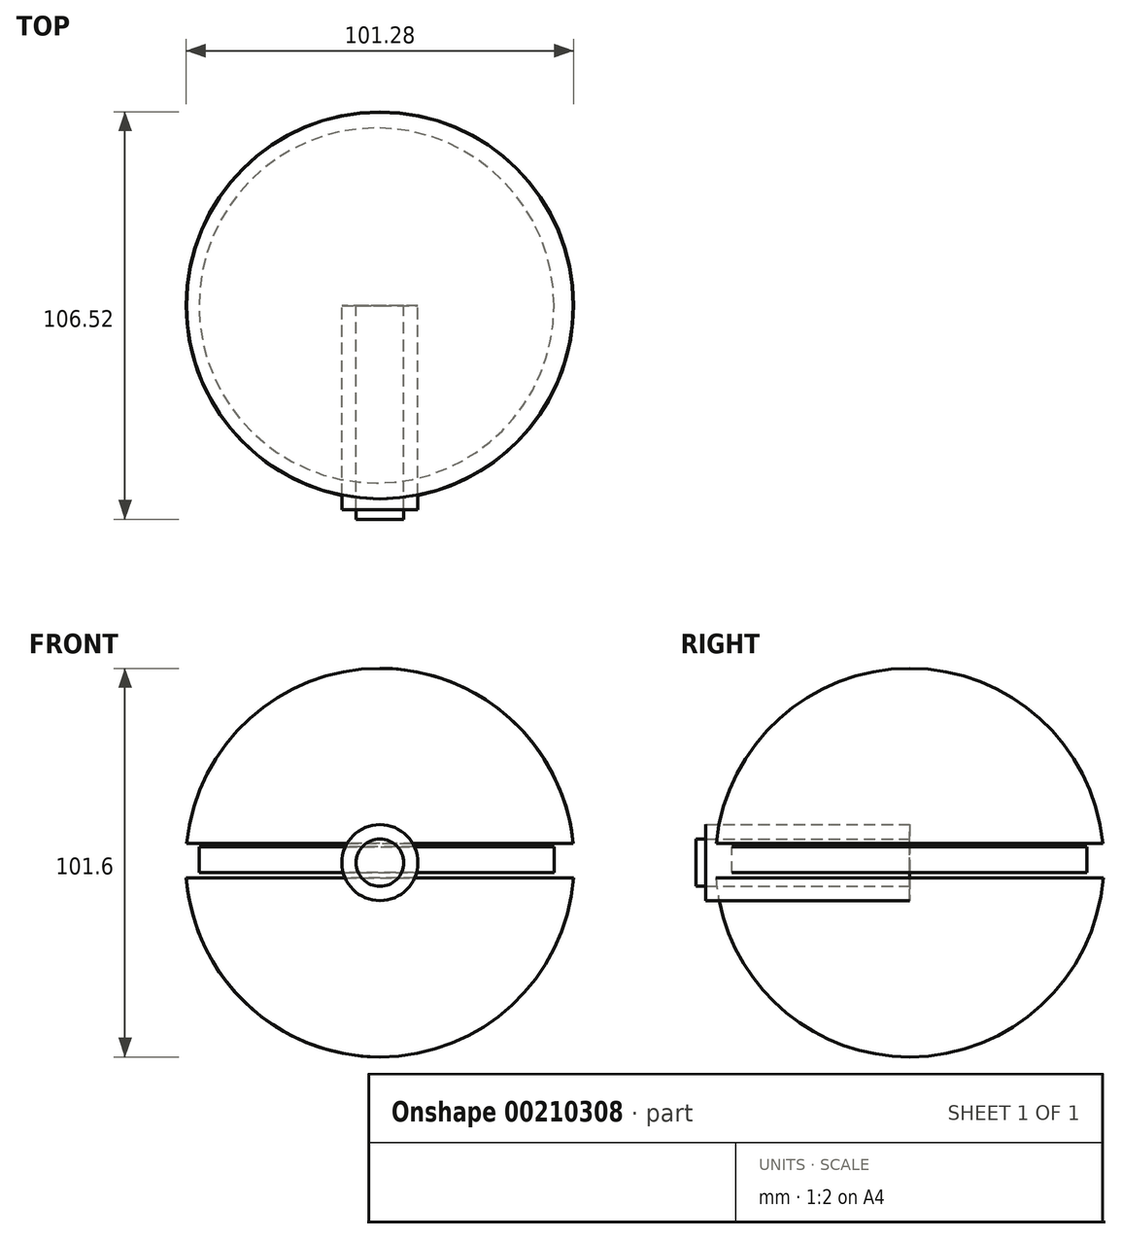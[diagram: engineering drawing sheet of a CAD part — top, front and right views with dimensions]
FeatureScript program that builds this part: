
annotation { "Feature Type Name" : "Feature", "Feature Type Description" : "" }
export const myFeature = defineFeature(function(context is Context, id is Id, definition is map)
    precondition{}
    {
        {
            var Q0;
            Q0=qCreatedBy(makeId("Front.planeOp"),FACE);
            var sketch = newSketch(context, id + "F0", { "sketchPlane" : qUnion([Q0])});
            skCircle(sketch, "E0", {"center": v(0, 0) * mm, "radius": 50.8 * mm});
            skLineSegment(sketch, "E1", {"start": v(-53.05, 5.08) * mm, "end": v(55.48, 5.08) * mm});
            skLineSegment(sketch, "E2", {"start": v(-52.82, -3.98) * mm, "end": v(55.03, -3.98) * mm});
            skLineSegment(sketch, "E3", {"start": v(0, 55.48) * mm, "end": v(0, -59.01) * mm});
            skSolve(sketch);
        }
        {
            var Q0;
            {var subQ0=sQuery(id+"F0.wireOp",EDGE,"E3");var subQ1=sQuery(id+"F0.wireOp",EDGE,"E0");var subQ2=makeQuery(id+"F0.imprint","INTERSECT",VERTEX,{"disambiguationData":[OD(0.0)],"derivedFrom":[subQ1,subQ0]});Q0=makeQuery(id+"F0.imprint","IMPRINT",FACE,{"disambiguationData":[TD([[makeQuery(id+"F0.imprint","IMPRINT",EDGE,{"disambiguationData":[TD([[subQ2,1.0]])],"derivedFrom":subQ1}),1.0]])]});}
            var Q1;
            {var subQ0=sQuery(id+"F0.wireOp",EDGE,"E2");var subQ1=sQuery(id+"F0.wireOp",EDGE,"E0");var subQ2=makeQuery(id+"F0.imprint","INTERSECT",VERTEX,{"disambiguationData":[OD(0.0)],"derivedFrom":[subQ1,subQ0]});Q1=makeQuery(id+"F0.imprint","IMPRINT",FACE,{"disambiguationData":[TD([[makeQuery(id+"F0.imprint","IMPRINT",EDGE,{"disambiguationData":[TD([[subQ2,-1.0]])],"derivedFrom":subQ1}),1.0]])]});}
            var Q2;
            Q2=sQuery(id+"F0.wireOp",EDGE,"E3");
            revolve(context, id + "F1", {"entities" : qUnion([Q0, Q1]), "axis" : qUnion([Q2]), "revolveType" : RevolveType.FULL});
        }
        {
            var Q0;
            Q0=qCreatedBy(makeId("Front.planeOp"),FACE);
            var sketch = newSketch(context, id + "F2", { "sketchPlane" : qUnion([Q0])});
            skLineSegment(sketch, "E4.bottom", {"start": v(-47.3, 4.2) * mm, "end": v(45.53, 4.2) * mm});
            skLineSegment(sketch, "E4.top", {"start": v(-47.3, -2.65) * mm, "end": v(45.53, -2.65) * mm});
            skLineSegment(sketch, "E4.left", {"start": v(-47.3, 4.2) * mm, "end": v(-47.3, -2.65) * mm});
            skLineSegment(sketch, "E4.right", {"start": v(45.53, 4.2) * mm, "end": v(45.53, -2.65) * mm});
            skLineSegment(sketch, "E5", {"start": v(-0.88, 4.2) * mm, "end": v(-0.88, -2.65) * mm});
            skSolve(sketch);
        }
        {
            var Q0;
            {var subQ0=sQuery(id+"F2.wireOp",EDGE,"E4.right");Q0=makeQuery(id+"F2.imprint","IMPRINT",FACE,{"disambiguationData":[TD([[makeQuery(id+"F2.imprint","IMPRINT",EDGE,{"derivedFrom":subQ0}),-1.0]])]});}
            var Q1;
            Q1=sQuery(id+"F2.wireOp",EDGE,"E5");
            revolve(context, id + "F3", {"entities" : qUnion([Q0]), "axis" : qUnion([Q1]), "revolveType" : RevolveType.FULL});
        }
        {
            var Q0;
            Q0=qCreatedBy(makeId("Front.planeOp"),FACE);
            var sketch = newSketch(context, id + "F4", { "sketchPlane" : qUnion([Q0])});
            skCircle(sketch, "E6", {"center": v(0, 0) * mm, "radius": 9.95 * mm});
            skSolve(sketch);
        }
        {
            var Q0;
            Q0=qCreatedBy(makeId("Front.planeOp"),FACE);
            var sketch = newSketch(context, id + "F5", { "sketchPlane" : qUnion([Q0])});
            skCircle(sketch, "E7", {"center": v(0, 0) * mm, "radius": 6.2 * mm});
            skSolve(sketch);
        }
        {
            var Q0;
            Q0 = qSketchRegion(id + "F4", true);
            extrude(context, id + "F6", {"entities" : qUnion([Q0]), "depth" : 53.34 * mm});
        }
        {
            var Q0;
            Q0 = qSketchRegion(id + "F5", true);
            extrude(context, id + "F7", {"entities" : qUnion([Q0]), "depth" : 55.88 * mm});
        }
    });
